# Revit family: Merida Dozownik mydła w płynie STELLA MAXI
name_source: partatom
category: Modele ogólne
revit_build: Autodesk Revit 2015 (Build: 20140606_1530(x64)
units: mm (PartAtom-declared; Revit-internal decimal feet)

## types (5) — shared parameters
Autor = www.archispace.pl
Domyślna rzędna = 900 mm  [stored 2.95276 ft]
Głębokość = 110 mm  [stored 0.360892 ft]
Karta techniczna produktu = https://sklep.merida.com.pl
Producent = MERIDA SP. Z O.O.
Rodzaj montażu = ścienny
Sposób dozowania = dozowanie ręczne
Strona produktu = https://sklep.merida.com.pl
Szerokość = 120 mm  [stored 0.393701 ft]
URL = www.merida.com.pl
Wielkość = MAXI
Wysokość = 262 mm  [stored 0.85958 ft]

## per-type parameters (varying)
| type | Kolor | Linia | Materiał obudowa | Materiał obudowy | Model | Opis | Pojemność | Typ mydła |
| DSM101 | matowa | MERIDA STELLA | Merida_Stal_Matowa | stal nierdzewna | Dozownik mydła w płynie Merida Stella Maxi, matowy | DSM101, dozownik mydła w płynie, stal nierdzewna matowa, montaż naścienny, łączenia boków spawane i szlifowane, niewidoczne zawiasy, metalowy zamek bębenkowy licowany z powierzchnią urządzenia, okienko kontroli poziomu mydła, zbiornik na mydło z tworzywa sztucznego, możliwość wyjęcia zbiornika ułatwia okresowe czyszczenie, mydło uzupełniane z kanistra | 0,8l | mydło w płynie |
| DSB101 | biały | MERIDA STELLA BIAŁA | Merida_biały_półmat | mosiądz chromowany | Dozownik mydła w płynie Merida Stella Maxi,  biały | DSB101, dozownik mydła w płynie, stal nierdzewna malowana proszkowo na biało, montaż naścienny, łączenia boków spawane, niewidoczne zawiasy, metalowy zamek bębenkowy licowany z powierzchnią urządzenia, okienko kontroli poziomu mydła, zbiornik na mydło z tworzywa sztucznego, możliwość wyjęcia zbiornika ułatwia okresowe czyszczenie, mydło uzupełniane z kanistra | 0,8l | mydło w płynie |
| DSM401 | matowa | MERIDA STELLA | Merida_Stal_Matowa | stal nierdzewna | Dozownik płynu dezynfekcyjnego Merida Stella Maxi matowy | DSM401, dozownik płynu dezynfekcyjnego, stal nierdzewna matowa, montaż naścienny, łączenia boków spawane i szlifowane, niewidoczne zawiasy, metalowy zamek bębenkowy licowany z powierzchnią urządzenia, okienko kontroli poziomu płynu, płyn w postaci mgiełki podawany z jednorazowego wkładu. | 1l | płyn dezynfekcyjny |
| DSP101 | polerowana | MERIDA STELLA | Merida_Stal_Polerowana | stal nierdzewna | Dozownik mydła w płynie Merida Stella Maxi polerowany | DSP101, dozownik mydła w płynie, stal nierdzewna polerowana, montaż naścienny, łączenia boków spawane i polerowane, niewidoczne zawiasy, metalowy zamek bębenkowy licowany z powierzchnią urządzenia, okienko kontroli poziomu mydła, zbiornik na mydło z tworzywa sztucznego, możliwość wyjęcia zbiornika ułatwia okresowe czyszczenie, mydło uzupełnia się z kanistra | 0,8l | mydło w płynie |
| DSP401 | polerowana | MERIDA STELLA | Merida_Stal_Matowa | stal nierdzewna | Dozownik płynu dezynfekcyjnego Merida Stella Maxi polerowany | DSP401, dozownik płynu dezynfekcyjnego, stal nierdzewna polerowana, montaż naścienny, łączenia boków spawane i polerowane, niewidoczne zawiasy, metalowy zamek bębenkowy licowany z powierzchnią urządzenia, okienko kontroli poziomu płynu, płyn w postaci mgiełki podawany z jednorazowego wkładu. | 1l | płyn dezynfekcyjny |

note: column(s) folded — value = type name in every type: Numer katalogowy

note: [stored X ft] marks values corroborated as IEEE doubles in the binary element streams (Revit-internal decimal feet)
